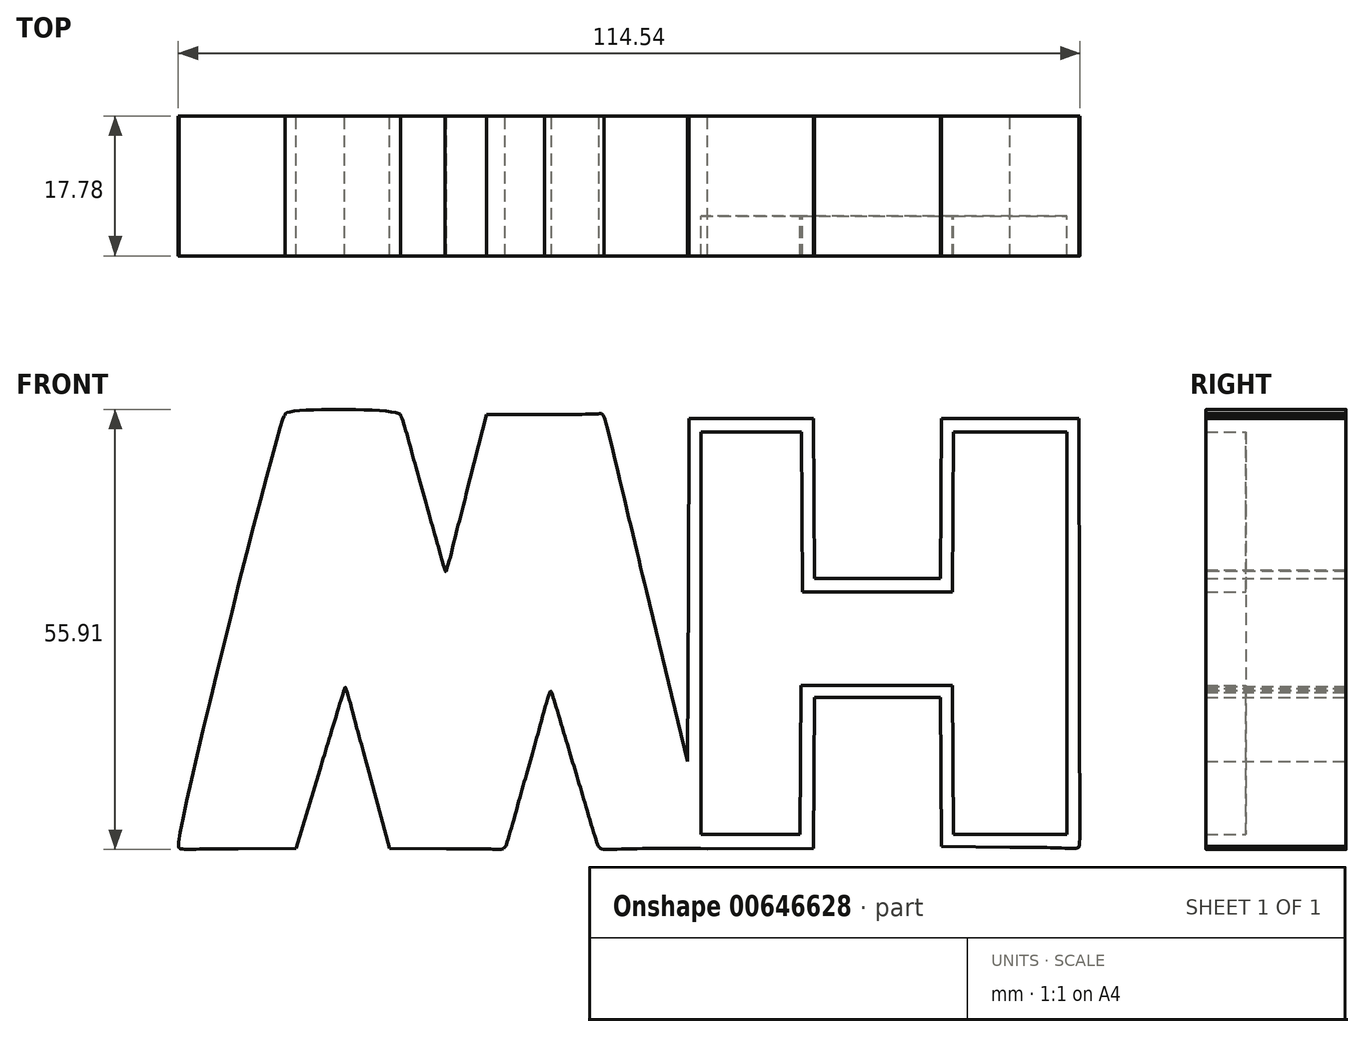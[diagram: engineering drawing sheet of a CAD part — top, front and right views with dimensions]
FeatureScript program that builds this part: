
annotation { "Feature Type Name" : "Feature", "Feature Type Description" : "" }
export const myFeature = defineFeature(function(context is Context, id is Id, definition is map)
    precondition{}
    {
        {
            var Q0;
            Q0=qCreatedBy(makeId("Front.planeOp"),FACE);
            var sketch = newSketch(context, id + "F0", { "sketchPlane" : qUnion([Q0])});
            skFitSpline(sketch, "E0", {"points": [v(-60.32, -22.29) * mm, v(-60.44, -22.1) * mm, v(-47.14, 32.2) * mm, v(-46.88, 32.61) * mm]});
            skFitSpline(sketch, "E1", {"points": [v(-46.88, 32.61) * mm, v(-46.66, 32.97) * mm, v(-32.47, 32.9) * mm, v(-32.2, 32.54) * mm]});
            skFitSpline(sketch, "E2", {"points": [v(-32.2, 32.54) * mm, v(-32.08, 32.38) * mm, v(-30.8, 28.02) * mm, v(-29.35, 22.84) * mm]});
            skFitSpline(sketch, "E3", {"points": [v(-29.35, 22.84) * mm, v(-27.9, 17.67) * mm, v(-26.65, 13.25) * mm, v(-26.57, 13.02) * mm]});
            skFitSpline(sketch, "E4", {"points": [v(-26.57, 13.02) * mm, v(-26.49, 12.8) * mm, v(-25.33, 16.92) * mm, v(-23.86, 22.66) * mm]});
            skFitSpline(sketch, "E5", {"points": [v(-13.94, 32.78) * mm, v(-7.12, 32.83) * mm, v(-6.58, 32.8) * mm, v(-6.38, 32.43) * mm]});
            skFitSpline(sketch, "E6", {"points": [v(-6.38, 32.43) * mm, v(-6.27, 32.2) * mm, v(-3.83, 22.26) * mm, v(-0.97, 10.34) * mm]});
            skLineSegment(sketch, "E7", {"start": v(-23.86, 22.66) * mm, "end": v(-21.29, 32.71) * mm});
            skLineSegment(sketch, "E8", {"start": v(-21.29, 32.71) * mm, "end": v(-13.94, 32.78) * mm});
            skFitSpline(sketch, "E9", {"points": [v(54, 5.18) * mm, v(54.04, -9.7) * mm, v(54.02, -21.99) * mm, v(53.98, -22.11) * mm]});
            skFitSpline(sketch, "E10", {"points": [v(53.98, -22.11) * mm, v(53.92, -22.27) * mm, v(50.89, -22.3) * mm, v(45.2, -22.23) * mm]});
            skLineSegment(sketch, "E11", {"start": v(-0.97, 10.34) * mm, "end": v(4.23, -11.34) * mm});
            skLineSegment(sketch, "E12", {"start": v(4.23, -11.34) * mm, "end": v(4.34, 10.45) * mm});
            skLineSegment(sketch, "E13", {"start": v(4.34, 10.45) * mm, "end": v(4.46, 32.25) * mm});
            skLineSegment(sketch, "E14", {"start": v(4.46, 32.25) * mm, "end": v(12.36, 32.25) * mm});
            skLineSegment(sketch, "E15", {"start": v(12.36, 32.25) * mm, "end": v(20.26, 32.25) * mm});
            skLineSegment(sketch, "E16", {"start": v(20.26, 32.25) * mm, "end": v(20.32, 22.09) * mm});
            skLineSegment(sketch, "E17", {"start": v(20.32, 22.09) * mm, "end": v(20.38, 11.92) * mm});
            skLineSegment(sketch, "E18", {"start": v(20.38, 11.92) * mm, "end": v(28.39, 11.92) * mm});
            skLineSegment(sketch, "E19", {"start": v(28.39, 11.92) * mm, "end": v(36.4, 11.92) * mm});
            skLineSegment(sketch, "E20", {"start": v(36.4, 11.92) * mm, "end": v(36.46, 22.09) * mm});
            skLineSegment(sketch, "E21", {"start": v(36.46, 22.09) * mm, "end": v(36.52, 32.25) * mm});
            skLineSegment(sketch, "E22", {"start": v(36.52, 32.25) * mm, "end": v(45.23, 32.25) * mm});
            skLineSegment(sketch, "E23", {"start": v(45.23, 32.25) * mm, "end": v(53.95, 32.25) * mm});
            skLineSegment(sketch, "E24", {"start": v(53.95, 32.25) * mm, "end": v(54, 5.18) * mm});
            skFitSpline(sketch, "E25", {"points": [v(6.76, -22.4) * mm, v(-3.87, -22.45) * mm, v(-6.8, -22.4) * mm, v(-6.98, -22.17) * mm]});
            skFitSpline(sketch, "E26", {"points": [v(-6.98, -22.17) * mm, v(-7.1, -22.01) * mm, v(-8.5, -17.6) * mm, v(-10.06, -12.36) * mm]});
            skFitSpline(sketch, "E27", {"points": [v(-10.06, -12.36) * mm, v(-11.63, -7.12) * mm, v(-12.98, -2.7) * mm, v(-13.06, -2.55) * mm]});
            skFitSpline(sketch, "E28", {"points": [v(-13.06, -2.55) * mm, v(-13.14, -2.4) * mm, v(-14.45, -6.68) * mm, v(-15.97, -12.07) * mm]});
            skFitSpline(sketch, "E29", {"points": [v(-15.97, -12.07) * mm, v(-17.48, -17.47) * mm, v(-18.83, -22.01) * mm, v(-18.95, -22.18) * mm]});
            skFitSpline(sketch, "E30", {"points": [v(-18.95, -22.18) * mm, v(-19.13, -22.4) * mm, v(-20.8, -22.46) * mm, v(-26.39, -22.4) * mm]});
            skLineSegment(sketch, "E31", {"start": v(45.2, -22.23) * mm, "end": v(36.52, -22.11) * mm});
            skLineSegment(sketch, "E32", {"start": v(36.52, -22.11) * mm, "end": v(36.46, -12.65) * mm});
            skLineSegment(sketch, "E33", {"start": v(36.46, -12.65) * mm, "end": v(36.4, -3.18) * mm});
            skLineSegment(sketch, "E34", {"start": v(36.4, -3.18) * mm, "end": v(28.39, -3.18) * mm});
            skLineSegment(sketch, "E35", {"start": v(28.39, -3.18) * mm, "end": v(20.38, -3.18) * mm});
            skLineSegment(sketch, "E36", {"start": v(20.38, -3.18) * mm, "end": v(20.32, -12.76) * mm});
            skLineSegment(sketch, "E37", {"start": v(20.32, -12.76) * mm, "end": v(20.26, -22.35) * mm});
            skLineSegment(sketch, "E38", {"start": v(20.26, -22.35) * mm, "end": v(6.76, -22.4) * mm});
            skFitSpline(sketch, "E39", {"points": [v(-36.4, -12.04) * mm, v(-37.94, -6.38) * mm, v(-39.25, -1.88) * mm, v(-39.3, -2.05) * mm]});
            skFitSpline(sketch, "E40", {"points": [v(-39.3, -2.05) * mm, v(-39.37, -2.23) * mm, v(-40.78, -6.86) * mm, v(-42.45, -12.36) * mm]});
            skLineSegment(sketch, "E41", {"start": v(-26.39, -22.4) * mm, "end": v(-33.6, -22.35) * mm});
            skLineSegment(sketch, "E42", {"start": v(-33.6, -22.35) * mm, "end": v(-36.4, -12.04) * mm});
            skFitSpline(sketch, "E43", {"points": [v(-52.85, -22.4) * mm, v(-56.9, -22.44) * mm, v(-60.26, -22.39) * mm, v(-60.32, -22.29) * mm]});
            skLineSegment(sketch, "E44", {"start": v(-42.45, -12.36) * mm, "end": v(-45.5, -22.35) * mm});
            skLineSegment(sketch, "E45", {"start": v(-45.5, -22.35) * mm, "end": v(-52.85, -22.4) * mm});
            skFitSpline(sketch, "E46", {"points": [v(-43.17, -8.46) * mm, v(-41.15, -1.79) * mm, v(-39.45, 3.76) * mm, v(-39.39, 3.87) * mm]});
            skFitSpline(sketch, "E47", {"points": [v(-39.39, 3.87) * mm, v(-39.33, 3.98) * mm, v(-39.17, 3.95) * mm, v(-39.03, 3.8) * mm]});
            skFitSpline(sketch, "E48", {"points": [v(-39.03, 3.8) * mm, v(-38.88, 3.67) * mm, v(-37.3, -1.86) * mm, v(-35.5, -8.47) * mm]});
            skFitSpline(sketch, "E49", {"points": [v(-16.82, -8.4) * mm, v(-14.94, -1.76) * mm, v(-13.32, 3.67) * mm, v(-13.2, 3.67) * mm]});
            skFitSpline(sketch, "E50", {"points": [v(-13.2, 3.67) * mm, v(-13.1, 3.67) * mm, v(-11.37, -1.76) * mm, v(-9.37, -8.4) * mm]});
            skLineSegment(sketch, "E51", {"start": v(-35.5, -8.47) * mm, "end": v(-32.22, -20.49) * mm});
            skLineSegment(sketch, "E52", {"start": v(-32.22, -20.49) * mm, "end": v(-26.22, -20.49) * mm});
            skLineSegment(sketch, "E53", {"start": v(-26.22, -20.49) * mm, "end": v(-20.23, -20.49) * mm});
            skLineSegment(sketch, "E54", {"start": v(-20.23, -20.49) * mm, "end": v(-16.82, -8.4) * mm});
            skFitSpline(sketch, "E55", {"points": [v(4.21, -19.5) * mm, v(4.13, -18.9) * mm, v(1.55, -8) * mm, v(-1.5, 4.72) * mm]});
            skFitSpline(sketch, "E56", {"points": [v(-1.5, 4.72) * mm, v(-4.56, 17.43) * mm, v(-7.22, 28.54) * mm, v(-7.42, 29.4) * mm]});
            skLineSegment(sketch, "E57", {"start": v(-9.37, -8.4) * mm, "end": v(-5.73, -20.49) * mm});
            skLineSegment(sketch, "E58", {"start": v(-5.73, -20.49) * mm, "end": v(-0.68, -20.55) * mm});
            skLineSegment(sketch, "E59", {"start": v(-0.68, -20.55) * mm, "end": v(4.37, -20.61) * mm});
            skLineSegment(sketch, "E60", {"start": v(4.37, -20.61) * mm, "end": v(4.21, -19.5) * mm});
            skFitSpline(sketch, "E61", {"points": [v(-22.98, 18.8) * mm, v(-24.68, 12.17) * mm, v(-26.17, 6.64) * mm, v(-26.3, 6.5) * mm]});
            skFitSpline(sketch, "E62", {"points": [v(-26.3, 6.5) * mm, v(-26.6, 6.2) * mm, v(-26.26, 5.1) * mm, v(-29.93, 18.2) * mm]});
            skFitSpline(sketch, "E63", {"points": [v(-29.93, 18.2) * mm, v(-31.66, 24.4) * mm, v(-33.19, 29.8) * mm, v(-33.32, 30.22) * mm]});
            skLineSegment(sketch, "E64", {"start": v(-7.42, 29.4) * mm, "end": v(-7.78, 30.98) * mm});
            skLineSegment(sketch, "E65", {"start": v(-7.78, 30.98) * mm, "end": v(-13.83, 30.92) * mm});
            skLineSegment(sketch, "E66", {"start": v(-13.83, 30.92) * mm, "end": v(-19.9, 30.86) * mm});
            skLineSegment(sketch, "E67", {"start": v(-19.9, 30.86) * mm, "end": v(-22.98, 18.8) * mm});
            skFitSpline(sketch, "E68", {"points": [v(-51.75, 5.6) * mm, v(-55.18, -8.37) * mm, v(-58.04, -19.97) * mm, v(-58.1, -20.2) * mm]});
            skFitSpline(sketch, "E69", {"points": [v(-58.1, -20.2) * mm, v(-58.2, -20.58) * mm, v(-57.82, -20.6) * mm, v(-52.53, -20.6) * mm]});
            skLineSegment(sketch, "E70", {"start": v(-33.32, 30.22) * mm, "end": v(-33.56, 30.97) * mm});
            skLineSegment(sketch, "E71", {"start": v(-33.56, 30.97) * mm, "end": v(-39.53, 30.97) * mm});
            skLineSegment(sketch, "E72", {"start": v(-39.53, 30.97) * mm, "end": v(-45.5, 30.97) * mm});
            skLineSegment(sketch, "E73", {"start": v(-45.5, 30.97) * mm, "end": v(-51.75, 5.6) * mm});
            skLineSegment(sketch, "E74", {"start": v(-52.53, -20.6) * mm, "end": v(-46.85, -20.6) * mm});
            skLineSegment(sketch, "E75", {"start": v(-46.85, -20.6) * mm, "end": v(-43.17, -8.46) * mm});
            skLineSegment(sketch, "E76", {"start": v(18.57, -11.14) * mm, "end": v(18.63, -1.67) * mm});
            skLineSegment(sketch, "E77", {"start": v(18.63, -1.67) * mm, "end": v(28.27, -1.67) * mm});
            skLineSegment(sketch, "E78", {"start": v(28.27, -1.67) * mm, "end": v(37.91, -1.67) * mm});
            skLineSegment(sketch, "E79", {"start": v(37.91, -1.67) * mm, "end": v(37.98, -11.14) * mm});
            skLineSegment(sketch, "E80", {"start": v(37.98, -11.14) * mm, "end": v(38.04, -20.6) * mm});
            skLineSegment(sketch, "E81", {"start": v(38.04, -20.6) * mm, "end": v(45.24, -20.6) * mm});
            skLineSegment(sketch, "E82", {"start": v(45.24, -20.6) * mm, "end": v(52.43, -20.6) * mm});
            skLineSegment(sketch, "E83", {"start": v(52.43, -20.6) * mm, "end": v(52.43, 4.95) * mm});
            skLineSegment(sketch, "E84", {"start": v(52.43, 4.95) * mm, "end": v(52.43, 30.5) * mm});
            skLineSegment(sketch, "E85", {"start": v(52.43, 30.5) * mm, "end": v(45.24, 30.5) * mm});
            skLineSegment(sketch, "E86", {"start": v(45.24, 30.5) * mm, "end": v(38.04, 30.5) * mm});
            skLineSegment(sketch, "E87", {"start": v(38.04, 30.5) * mm, "end": v(37.98, 20.34) * mm});
            skLineSegment(sketch, "E88", {"start": v(37.98, 20.34) * mm, "end": v(37.91, 10.18) * mm});
            skLineSegment(sketch, "E89", {"start": v(37.91, 10.18) * mm, "end": v(28.39, 10.18) * mm});
            skLineSegment(sketch, "E90", {"start": v(28.39, 10.18) * mm, "end": v(18.86, 10.18) * mm});
            skLineSegment(sketch, "E91", {"start": v(18.86, 10.18) * mm, "end": v(18.8, 20.34) * mm});
            skLineSegment(sketch, "E92", {"start": v(18.8, 20.34) * mm, "end": v(18.74, 30.5) * mm});
            skLineSegment(sketch, "E93", {"start": v(18.74, 30.5) * mm, "end": v(12.36, 30.5) * mm});
            skLineSegment(sketch, "E94", {"start": v(12.36, 30.5) * mm, "end": v(5.97, 30.5) * mm});
            skLineSegment(sketch, "E95", {"start": v(5.97, 30.5) * mm, "end": v(5.97, 4.95) * mm});
            skLineSegment(sketch, "E96", {"start": v(5.97, 4.95) * mm, "end": v(5.97, -20.6) * mm});
            skLineSegment(sketch, "E97", {"start": v(5.97, -20.6) * mm, "end": v(12.24, -20.6) * mm});
            skLineSegment(sketch, "E98", {"start": v(12.24, -20.6) * mm, "end": v(18.51, -20.6) * mm});
            skLineSegment(sketch, "E99", {"start": v(18.51, -20.6) * mm, "end": v(18.57, -11.14) * mm});
            skSolve(sketch);
        }
        {
            var Q0;
            Q0=makeQuery(id+"F0.imprint","IMPRINT",FACE,{"disambiguationData":[TD([[makeQuery(id+"F0.imprint","IMPRINT",EDGE,{"derivedFrom":sQuery(id+"F0.wireOp",EDGE,"E0")}),-1.0]])]});
            extrude(context, id + "F1", {"entities" : qUnion([Q0]), "depth" : 17.78 * mm, "offsetDistance" : 25.4 * mm});
        }
        {
            var Q0;
            Q0=makeQuery(id+"F0.imprint","IMPRINT",FACE,{"disambiguationData":[TD([[makeQuery(id+"F0.imprint","IMPRINT",EDGE,{"derivedFrom":sQuery(id+"F0.wireOp",EDGE,"E46")}),1.0]])]});
            var Q1;
            Q1=makeQuery(id+"F0.imprint","IMPRINT",FACE,{"disambiguationData":[TD([[makeQuery(id+"F0.imprint","IMPRINT",EDGE,{"derivedFrom":sQuery(id+"F0.wireOp",EDGE,"E76")}),1.0]])]});
            extrude(context, id + "F2", {"entities" : qUnion([Q0, Q1]), "operationType" : NewBodyOperationType.ADD, "depth" : 12.7 * mm, "offsetDistance" : 25.4 * mm});
        }
    });
